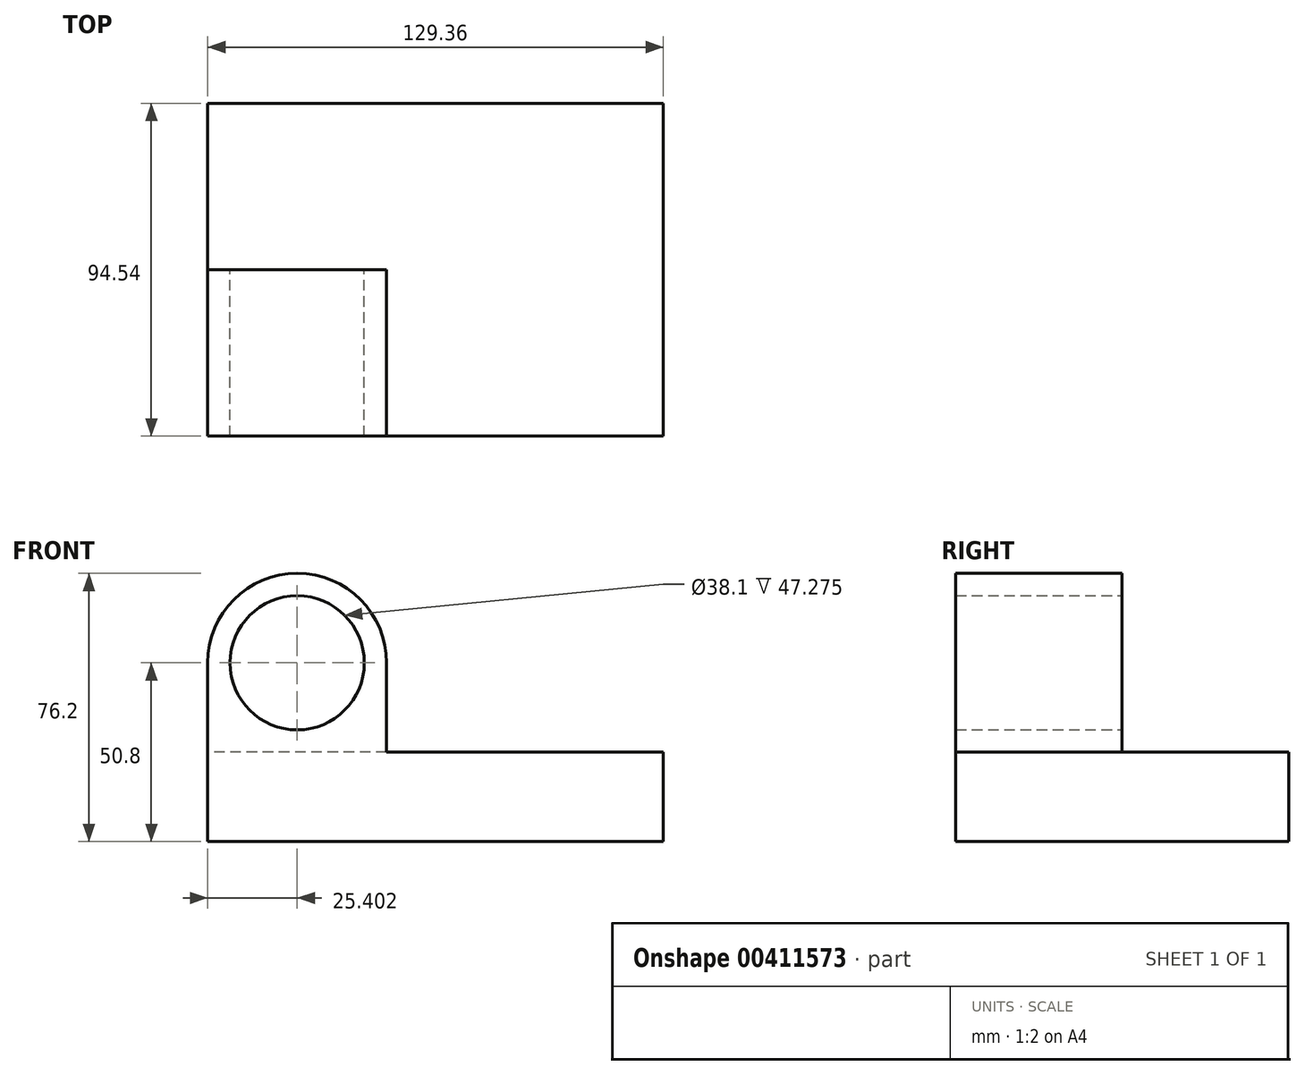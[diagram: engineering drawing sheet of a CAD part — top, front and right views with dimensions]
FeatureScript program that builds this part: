
annotation { "Feature Type Name" : "Feature", "Feature Type Description" : "" }
export const myFeature = defineFeature(function(context is Context, id is Id, definition is map)
    precondition{}
    {
        {
            var Q0;
            Q0=qCreatedBy(makeId("Top.planeOp"),FACE);
            var sketch = newSketch(context, id + "F0", { "sketchPlane" : qUnion([Q0])});
            skLineSegment(sketch, "E0.bottom", {"start": v(64.68, -47.27) * mm, "end": v(-64.68, -47.27) * mm});
            skLineSegment(sketch, "E0.top", {"start": v(64.68, 47.27) * mm, "end": v(-64.68, 47.27) * mm});
            skLineSegment(sketch, "E0.left", {"start": v(64.68, -47.27) * mm, "end": v(64.68, 47.27) * mm});
            skLineSegment(sketch, "E0.right", {"start": v(-64.68, -47.27) * mm, "end": v(-64.68, 47.27) * mm});
            skPoint(sketch, "E0.middle", {"position": v(0, 0) * mm});
            skSolve(sketch);
        }
        {
            var Q0;
            Q0 = qSketchRegion(id + "F0", true);
            extrude(context, id + "F1", {"entities" : qUnion([Q0]), "depth" : 25.4 * mm});
        }
        {
            var Q0;
            Q0=qCreatedBy(makeId("Front.planeOp"),FACE);
            var sketch = newSketch(context, id + "F2", { "sketchPlane" : qUnion([Q0])});
            skCircle(sketch, "E1", {"center": v(-39.28, 50.8) * mm, "radius": 19.05 * mm});
            skArc(sketch, "E2.0", {"start": v(-13.88, 50.8) * mm, "mid": v(-39.28, 76.2) * mm, "end": v(-64.68, 50.8) * mm});
            skLineSegment(sketch, "E3", {"start": v(-13.88, 50.8) * mm, "end": v(-13.88, 25.4) * mm});
            skLineSegment(sketch, "E4", {"start": v(-64.68, 50.8) * mm, "end": v(-64.68, 25.4) * mm});
            skLineSegment(sketch, "E5.0", {"start": v(64.68, 25.4) * mm, "end": v(-64.68, 25.4) * mm, "construction": true});
            skLineSegment(sketch, "E6", {"start": v(-13.88, 25.4) * mm, "end": v(-64.68, 25.4) * mm});
            skSolve(sketch);
        }
        {
            var Q0;
            Q0 = qSketchRegion(id + "F2", true);
            var Q1;
            Q1=makeQuery(id+"F1.opExtrude","SWEPT_FACE",FACE,{"disambiguationData":[OSD([sQuery(id+"F0.wireOp",EDGE,"E0.bottom")])]});
            extrude(context, id + "F3", {"entities" : qUnion([Q0]), "operationType" : NewBodyOperationType.ADD, "endBound" : BoundingType.UP_TO_SURFACE, "endBoundEntityFace" : qUnion([Q1]), "depth" : 25.4 * mm});
        }
    });
